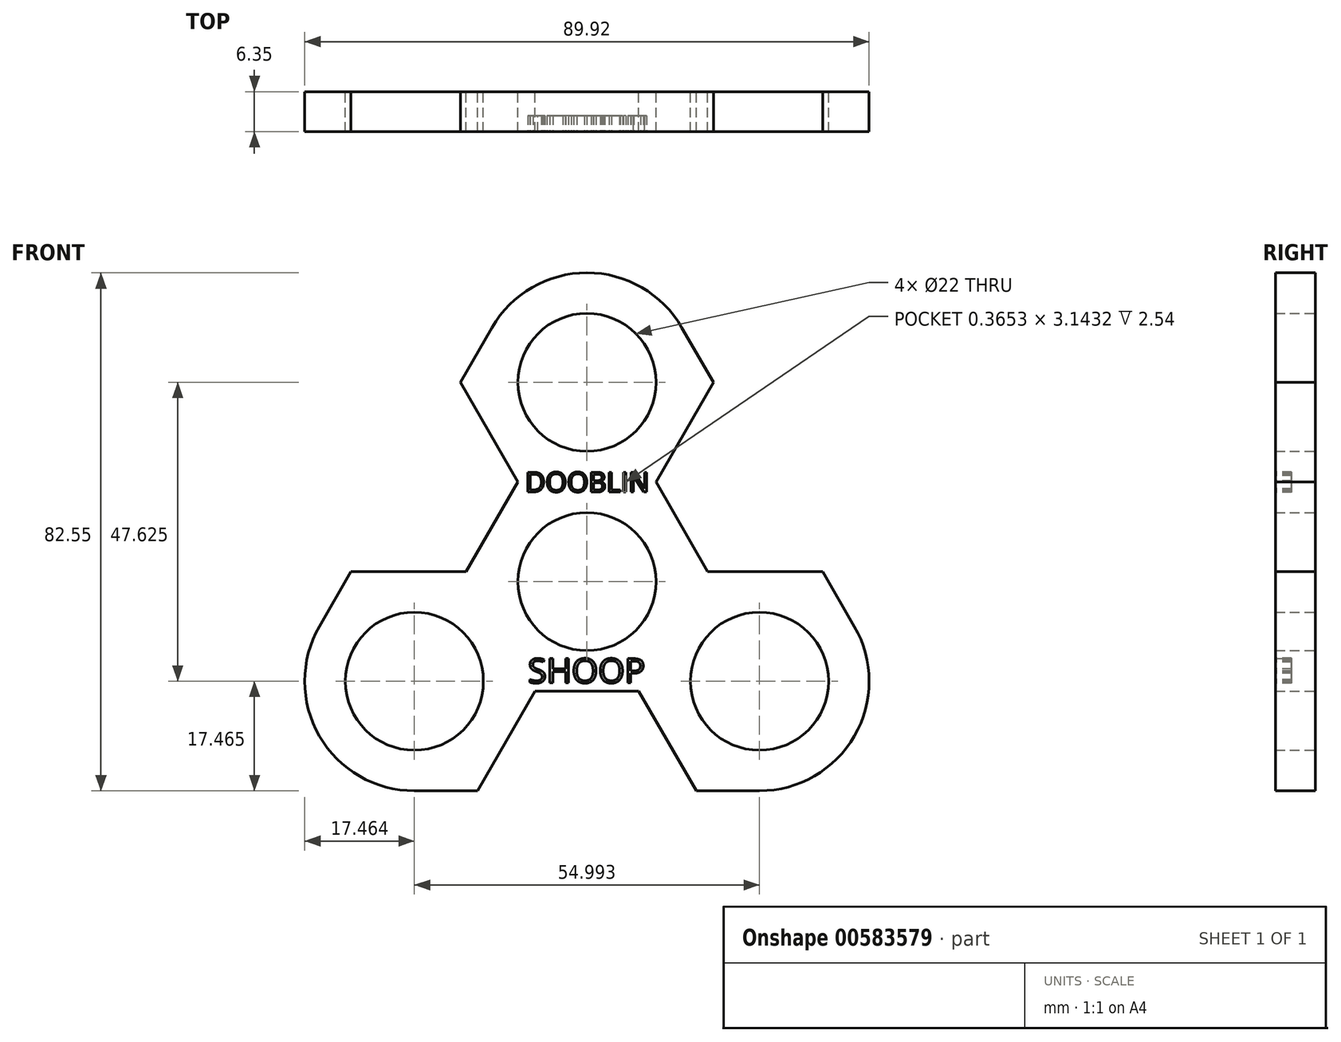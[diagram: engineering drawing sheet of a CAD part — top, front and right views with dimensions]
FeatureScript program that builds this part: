
annotation { "Feature Type Name" : "Feature", "Feature Type Description" : "" }
export const myFeature = defineFeature(function(context is Context, id is Id, definition is map)
    precondition{}
    {
        {
            var Q0;
            Q0=qCreatedBy(makeId("Front.planeOp"),FACE);
            var sketch = newSketch(context, id + "F0", { "sketchPlane" : qUnion([Q0])});
            skCircle(sketch, "E0", {"center": v(0, 0) * mm, "radius": 11 * mm});
            skCircle(sketch, "E1", {"center": v(0, 0) * mm, "radius": 14.29 * mm});
            skLineSegment(sketch, "E2", {"start": v(0, 0) * mm, "end": v(0, 31.75) * mm});
            skCircle(sketch, "E3", {"center": v(0, 31.75) * mm, "radius": 11 * mm});
            skCircle(sketch, "E4", {"center": v(0, 31.75) * mm, "radius": 14.29 * mm});
            skCircle(sketch, "E5.1.0", {"center": v(-27.5, -15.87) * mm, "radius": 11 * mm});
            skCircle(sketch, "E5.1.1", {"center": v(-27.5, -15.87) * mm, "radius": 14.29 * mm});
            skCircle(sketch, "E5.2.0", {"center": v(27.5, -15.88) * mm, "radius": 11 * mm});
            skCircle(sketch, "E5.2.1", {"center": v(27.5, -15.88) * mm, "radius": 14.29 * mm});
            skSolve(sketch);
        }
        {
            var Q0;
            Q0=qCreatedBy(makeId("Front.planeOp"),FACE);
            var sketch = newSketch(context, id + "F1", { "sketchPlane" : qUnion([Q0])});
            skCircle(sketch, "E6.0", {"center": v(0, 31.75) * mm, "radius": 14.29 * mm});
            skCircle(sketch, "E7.0", {"center": v(-27.5, -15.87) * mm, "radius": 14.29 * mm});
            skCircle(sketch, "E8.0", {"center": v(27.5, -15.88) * mm, "radius": 14.29 * mm});
            skCircle(sketch, "E9.0", {"center": v(0, 0) * mm, "radius": 14.29 * mm});
            skLineSegment(sketch, "E10.0", {"start": v(-10.08, 17.46) * mm, "end": v(-10.04, 17.46) * mm});
            skLineSegment(sketch, "E10.1", {"start": v(11, 15.88) * mm, "end": v(19.25, 1.59) * mm});
            skLineSegment(sketch, "E10.2", {"start": v(20.16, 0) * mm, "end": v(20.14, -0.04) * mm});
            skLineSegment(sketch, "E10.3", {"start": v(8.25, -17.46) * mm, "end": v(-8.25, -17.46) * mm});
            skLineSegment(sketch, "E10.4", {"start": v(-10.08, -17.46) * mm, "end": v(-10.1, -17.43) * mm});
            skLineSegment(sketch, "E10.5", {"start": v(-19.25, 1.59) * mm, "end": v(-11, 15.87) * mm});
            skPoint(sketch, "E10.0.midPoint", {"position": v(0, 17.46) * mm});
            skLineSegment(sketch, "E11.0", {"start": v(10.08, 14.29) * mm, "end": v(10.04, 14.29) * mm});
            skLineSegment(sketch, "E11.1", {"start": v(-11, 15.87) * mm, "end": v(-20.16, 31.75) * mm});
            skLineSegment(sketch, "E11.2", {"start": v(-20.16, 31.75) * mm, "end": v(-10.08, 49.21) * mm});
            skLineSegment(sketch, "E11.3", {"start": v(-10.08, 49.21) * mm, "end": v(10.08, 49.21) * mm});
            skLineSegment(sketch, "E11.4", {"start": v(10.08, 49.21) * mm, "end": v(20.16, 31.75) * mm});
            skLineSegment(sketch, "E11.5", {"start": v(20.16, 31.75) * mm, "end": v(11, 15.88) * mm});
            skPoint(sketch, "E11.0.midPoint", {"position": v(0, 14.29) * mm});
            skLineSegment(sketch, "E12.0", {"start": v(-17.41, 1.59) * mm, "end": v(-17.4, 1.55) * mm});
            skLineSegment(sketch, "E12.1", {"start": v(-8.25, -17.46) * mm, "end": v(-17.41, -33.34) * mm});
            skLineSegment(sketch, "E12.2", {"start": v(-17.41, -33.34) * mm, "end": v(-37.58, -33.34) * mm});
            skLineSegment(sketch, "E12.3", {"start": v(-37.58, -33.34) * mm, "end": v(-47.66, -15.88) * mm});
            skLineSegment(sketch, "E12.4", {"start": v(-47.66, -15.88) * mm, "end": v(-37.58, 1.59) * mm});
            skLineSegment(sketch, "E12.5", {"start": v(-37.58, 1.59) * mm, "end": v(-19.25, 1.59) * mm});
            skPoint(sketch, "E12.0.midPoint", {"position": v(-12.37, -7.14) * mm});
            skLineSegment(sketch, "E13.0", {"start": v(7.33, -15.88) * mm, "end": v(7.35, -15.84) * mm});
            skLineSegment(sketch, "E13.1", {"start": v(19.25, 1.59) * mm, "end": v(37.58, 1.59) * mm});
            skLineSegment(sketch, "E13.2", {"start": v(37.58, 1.59) * mm, "end": v(47.66, -15.88) * mm});
            skLineSegment(sketch, "E13.3", {"start": v(47.66, -15.88) * mm, "end": v(37.58, -33.34) * mm});
            skLineSegment(sketch, "E13.4", {"start": v(37.58, -33.34) * mm, "end": v(17.41, -33.34) * mm});
            skLineSegment(sketch, "E13.5", {"start": v(17.41, -33.34) * mm, "end": v(8.25, -17.46) * mm});
            skPoint(sketch, "E13.0.midPoint", {"position": v(12.37, -7.14) * mm});
            skLineSegment(sketch, "E14.trimOffspring", {"start": v(-10.04, 14.29) * mm, "end": v(-10.08, 14.29) * mm});
            skLineSegment(sketch, "E15.trimOffspring", {"start": v(10.04, 17.46) * mm, "end": v(10.08, 17.46) * mm});
            skLineSegment(sketch, "E16.trimOffspring", {"start": v(10.1, -17.43) * mm, "end": v(10.08, -17.46) * mm});
            skLineSegment(sketch, "E17.trimOffspring", {"start": v(17.4, 1.55) * mm, "end": v(17.41, 1.59) * mm});
            skLineSegment(sketch, "E18.trimOffspring", {"start": v(-20.14, -0.04) * mm, "end": v(-20.16, 0) * mm});
            skLineSegment(sketch, "E19.trimOffspring", {"start": v(-7.35, -15.84) * mm, "end": v(-7.33, -15.87) * mm});
            skSolve(sketch);
        }
        {
            var Q0;
            Q0 = qSketchRegion(id + "F1", true);
            extrude(context, id + "F2", {"entities" : qUnion([Q0]), "depth" : 6.35 * mm, "offsetDistance" : 25.4 * mm});
        }
        {
            var Q0;
            Q0=makeQuery(id+"F2.opExtrude","CAP_FACE",FACE,{"disambiguationData":[OSD([sQuery(id+"F1.wireOp",EDGE,"E6.0"),sQuery(id+"F1.wireOp",EDGE,"E7.0"),sQuery(id+"F1.wireOp",EDGE,"E8.0"),sQuery(id+"F1.wireOp",EDGE,"E9.0"),sQuery(id+"F1.wireOp",EDGE,"E10.1"),sQuery(id+"F1.wireOp",EDGE,"E10.3"),sQuery(id+"F1.wireOp",EDGE,"E10.5"),sQuery(id+"F1.wireOp",EDGE,"E11.1"),sQuery(id+"F1.wireOp",EDGE,"E11.2"),sQuery(id+"F1.wireOp",EDGE,"E11.3"),sQuery(id+"F1.wireOp",EDGE,"E11.4"),sQuery(id+"F1.wireOp",EDGE,"E11.5"),sQuery(id+"F1.wireOp",EDGE,"E12.1"),sQuery(id+"F1.wireOp",EDGE,"E12.2"),sQuery(id+"F1.wireOp",EDGE,"E12.3"),sQuery(id+"F1.wireOp",EDGE,"E12.4"),sQuery(id+"F1.wireOp",EDGE,"E12.5"),sQuery(id+"F1.wireOp",EDGE,"E13.1"),sQuery(id+"F1.wireOp",EDGE,"E13.2"),sQuery(id+"F1.wireOp",EDGE,"E13.3"),sQuery(id+"F1.wireOp",EDGE,"E13.4"),sQuery(id+"F1.wireOp",EDGE,"E13.5")])],"isStart":false});
            var sketch = newSketch(context, id + "F3", { "sketchPlane" : qUnion([Q0])});
            skText(sketch, "E20", { "text": "DOOBLIN", "fontName": "OpenSans-Regular.ttf"});
            skLineSegment(sketch, "E21", {"start": v(0, 15.88) * mm, "end": v(0, 15.88) * mm});
            skLineSegment(sketch, "E22", {"start": v(0, 14.29) * mm, "end": v(0, 17.46) * mm});
            skLineSegment(sketch, "E23", {"start": v(0, 17.46) * mm, "end": v(0, 14.29) * mm});
            skLineSegment(sketch, "E24", {"start": v(0, 14.29) * mm, "end": v(0, 12.01) * mm});
            skLineSegment(sketch, "E25", {"start": v(0, 12.01) * mm, "end": v(0, 17.46) * mm});
            skLineSegment(sketch, "E26.0", {"start": v(0, 0) * mm, "end": v(0, 31.75) * mm});
            const initialGuessF3  = {"E20": [-0.00982, 0.01429, 1, 0, 0.00317]};
            skSetInitialGuess(sketch, initialGuessF3);
            skSolve(sketch);
        }
        {
            var Q0;
            Q0 = qSketchRegion(id + "F3", true);
            extrude(context, id + "F4", {"entities" : qUnion([Q0]), "operationType" : NewBodyOperationType.REMOVE, "oppositeDirection" : true, "depth" : 2.54 * mm, "offsetDistance" : 25.4 * mm});
        }
        {
            var Q0;
            {var subQ0=sQuery(id+"F1.wireOp",EDGE,"E13.5");var subQ1=sQuery(id+"F1.wireOp",EDGE,"E13.4");var subQ2=sQuery(id+"F1.wireOp",EDGE,"E13.3");var subQ3=sQuery(id+"F1.wireOp",EDGE,"E12.5");var subQ4=sQuery(id+"F1.wireOp",EDGE,"E11.2");var subQ5=sQuery(id+"F1.wireOp",EDGE,"E11.1");var subQ6=sQuery(id+"F1.wireOp",EDGE,"E10.5");var subQ7=sQuery(id+"F1.wireOp",EDGE,"E10.3");var subQ8=sQuery(id+"F1.wireOp",EDGE,"E10.1");var subQ9=sQuery(id+"F1.wireOp",EDGE,"E11.3");var subQ10=sQuery(id+"F1.wireOp",EDGE,"E6.0");var subQ11=sQuery(id+"F1.wireOp",EDGE,"E9.0");var subQ12=sQuery(id+"F1.wireOp",EDGE,"E7.0");var subQ13=sQuery(id+"F1.wireOp",EDGE,"E8.0");var subQ14=sQuery(id+"F1.wireOp",EDGE,"E11.4");var subQ15=sQuery(id+"F1.wireOp",EDGE,"E11.5");var subQ16=sQuery(id+"F1.wireOp",EDGE,"E12.1");var subQ17=sQuery(id+"F1.wireOp",EDGE,"E12.2");var subQ18=sQuery(id+"F1.wireOp",EDGE,"E12.3");var subQ19=sQuery(id+"F1.wireOp",EDGE,"E12.4");var subQ20=sQuery(id+"F1.wireOp",EDGE,"E13.1");var subQ21=sQuery(id+"F1.wireOp",EDGE,"E13.2");Q0=makeQuery(id+"F4.boolean.opBoolean","SPLIT",FACE,{"disambiguationData":[TD([makeQuery(id+"F2.opExtrude","SWEPT_FACE",FACE,{"disambiguationData":[OSD([subQ10])]})])],"derivedFrom":makeQuery(id+"F2.opExtrude","CAP_FACE",FACE,{"disambiguationData":[OSD([subQ10,subQ12,subQ13,subQ11,subQ8,subQ7,subQ6,subQ5,subQ4,subQ9,subQ14,subQ15,subQ16,subQ17,subQ18,subQ19,subQ3,subQ20,subQ21,subQ2,subQ1,subQ0])],"isStart":false})});}
            var sketch = newSketch(context, id + "F5", { "sketchPlane" : qUnion([Q0])});
            skCircle(sketch, "E27", {"center": v(0, 31.75) * mm, "radius": 17.46 * mm});
            skCircle(sketch, "E28", {"center": v(-27.5, -15.87) * mm, "radius": 17.46 * mm});
            skCircle(sketch, "E29", {"center": v(27.5, -15.88) * mm, "radius": 17.46 * mm});
            skSolve(sketch);
        }
        {
            var Q0;
            {var subQ0=sQuery(id+"F5.wireOp",EDGE,"E27");var subQ1=makeQuery(id+"F2.opExtrude","CAP_EDGE",EDGE,{"disambiguationData":[OSD([sQuery(id+"F1.wireOp",EDGE,"E11.3")])],"isStart":false});var subQ2=makeQuery(id+"F5.imprint","INTERSECT",VERTEX,{"derivedFrom":[subQ1,subQ0]});Q0=makeQuery(id+"F5.imprint","IMPRINT",FACE,{"disambiguationData":[TD([[makeQuery(id+"F5.imprint","IMPRINT",EDGE,{"disambiguationData":[TD([[subQ2,-1.0]])],"derivedFrom":subQ0}),-1.0]])]});}
            var Q1;
            {var subQ0=sQuery(id+"F5.wireOp",EDGE,"E27");var subQ1=makeQuery(id+"F2.opExtrude","CAP_EDGE",EDGE,{"disambiguationData":[OSD([sQuery(id+"F1.wireOp",EDGE,"E11.3")])],"isStart":false});var subQ2=makeQuery(id+"F5.imprint","INTERSECT",VERTEX,{"derivedFrom":[subQ1,subQ0]});Q1=makeQuery(id+"F5.imprint","IMPRINT",FACE,{"disambiguationData":[TD([[makeQuery(id+"F5.imprint","IMPRINT",EDGE,{"disambiguationData":[TD([[subQ2,1.0]])],"derivedFrom":subQ0}),-1.0]])]});}
            var Q2;
            {var subQ0=sQuery(id+"F5.wireOp",EDGE,"E28");var subQ1=makeQuery(id+"F2.opExtrude","CAP_EDGE",EDGE,{"disambiguationData":[OSD([sQuery(id+"F1.wireOp",EDGE,"E12.4")])],"isStart":false});var subQ2=makeQuery(id+"F5.imprint","INTERSECT",VERTEX,{"derivedFrom":[subQ1,subQ0]});Q2=makeQuery(id+"F5.imprint","IMPRINT",FACE,{"disambiguationData":[TD([[makeQuery(id+"F5.imprint","IMPRINT",EDGE,{"disambiguationData":[TD([[subQ2,-1.0]])],"derivedFrom":subQ0}),-1.0]])]});}
            var Q3;
            {var subQ0=sQuery(id+"F5.wireOp",EDGE,"E28");var subQ1=makeQuery(id+"F2.opExtrude","CAP_EDGE",EDGE,{"disambiguationData":[OSD([sQuery(id+"F1.wireOp",EDGE,"E12.3")])],"isStart":false});var subQ2=makeQuery(id+"F5.imprint","INTERSECT",VERTEX,{"derivedFrom":[subQ1,subQ0]});Q3=makeQuery(id+"F5.imprint","IMPRINT",FACE,{"disambiguationData":[TD([[makeQuery(id+"F5.imprint","IMPRINT",EDGE,{"disambiguationData":[TD([[subQ2,-1.0]])],"derivedFrom":subQ0}),-1.0]])]});}
            var Q4;
            {var subQ0=sQuery(id+"F5.wireOp",EDGE,"E29");var subQ1=makeQuery(id+"F2.opExtrude","CAP_EDGE",EDGE,{"disambiguationData":[OSD([sQuery(id+"F1.wireOp",EDGE,"E13.4")])],"isStart":false});var subQ2=makeQuery(id+"F5.imprint","INTERSECT",VERTEX,{"derivedFrom":[subQ1,subQ0]});Q4=makeQuery(id+"F5.imprint","IMPRINT",FACE,{"disambiguationData":[TD([[makeQuery(id+"F5.imprint","IMPRINT",EDGE,{"disambiguationData":[TD([[subQ2,-1.0]])],"derivedFrom":subQ0}),-1.0]])]});}
            var Q5;
            {var subQ0=sQuery(id+"F5.wireOp",EDGE,"E29");var subQ1=makeQuery(id+"F2.opExtrude","CAP_EDGE",EDGE,{"disambiguationData":[OSD([sQuery(id+"F1.wireOp",EDGE,"E13.2")])],"isStart":false});var subQ2=makeQuery(id+"F5.imprint","INTERSECT",VERTEX,{"derivedFrom":[subQ1,subQ0]});Q5=makeQuery(id+"F5.imprint","IMPRINT",FACE,{"disambiguationData":[TD([[makeQuery(id+"F5.imprint","IMPRINT",EDGE,{"disambiguationData":[TD([[subQ2,1.0]])],"derivedFrom":subQ0}),-1.0]])]});}
            extrude(context, id + "F6", {"entities" : qUnion([Q0, Q1, Q2, Q3, Q4, Q5]), "operationType" : NewBodyOperationType.REMOVE, "oppositeDirection" : true, "depth" : 25.4 * mm, "offsetDistance" : 25.4 * mm});
        }
        {
            var Q0;
            Q0=makeQuery(id+"F0.imprint","IMPRINT",FACE,{"disambiguationData":[TD([[makeQuery(id+"F0.imprint","IMPRINT",EDGE,{"derivedFrom":sQuery(id+"F0.wireOp",EDGE,"E3")}),-1.0]])]});
            var sketch = newSketch(context, id + "F7", { "sketchPlane" : qUnion([Q0])});
            skSolve(sketch);
        }
        {
            var Q0;
            Q0 = qSketchRegion(id + "F7", true);
            var Q1;
            Q1=makeQuery(id+"F0.imprint","IMPRINT",FACE,{"disambiguationData":[TD([[makeQuery(id+"F0.imprint","IMPRINT",EDGE,{"derivedFrom":sQuery(id+"F0.wireOp",EDGE,"E5.1.0")}),-1.0]])]});
            var Q2;
            Q2=makeQuery(id+"F0.imprint","IMPRINT",FACE,{"disambiguationData":[TD([[makeQuery(id+"F0.imprint","IMPRINT",EDGE,{"derivedFrom":sQuery(id+"F0.wireOp",EDGE,"E0")}),-1.0]])]});
            var Q3;
            Q3=makeQuery(id+"F0.imprint","IMPRINT",FACE,{"disambiguationData":[TD([[makeQuery(id+"F0.imprint","IMPRINT",EDGE,{"derivedFrom":sQuery(id+"F0.wireOp",EDGE,"E5.2.0")}),-1.0]])]});
            var Q4;
            Q4=makeQuery(id+"F0.imprint","IMPRINT",FACE,{"disambiguationData":[TD([[makeQuery(id+"F0.imprint","IMPRINT",EDGE,{"derivedFrom":sQuery(id+"F0.wireOp",EDGE,"E3")}),-1.0]])]});
            extrude(context, id + "F8", {"entities" : qUnion([Q0, Q1, Q2, Q3, Q4]), "operationType" : NewBodyOperationType.ADD, "depth" : 6.35 * mm, "offsetDistance" : 25.4 * mm});
        }
        {
            var Q0;
            {var subQ0=sQuery(id+"F1.wireOp",EDGE,"E13.5");var subQ1=sQuery(id+"F1.wireOp",EDGE,"E13.4");var subQ2=sQuery(id+"F1.wireOp",EDGE,"E13.3");var subQ3=sQuery(id+"F1.wireOp",EDGE,"E12.5");var subQ4=sQuery(id+"F1.wireOp",EDGE,"E11.2");var subQ5=sQuery(id+"F1.wireOp",EDGE,"E11.1");var subQ6=sQuery(id+"F1.wireOp",EDGE,"E10.5");var subQ7=sQuery(id+"F1.wireOp",EDGE,"E10.3");var subQ8=sQuery(id+"F1.wireOp",EDGE,"E10.1");var subQ9=sQuery(id+"F1.wireOp",EDGE,"E11.3");var subQ10=sQuery(id+"F1.wireOp",EDGE,"E6.0");var subQ11=sQuery(id+"F1.wireOp",EDGE,"E9.0");var subQ12=sQuery(id+"F1.wireOp",EDGE,"E7.0");var subQ13=sQuery(id+"F1.wireOp",EDGE,"E8.0");var subQ14=sQuery(id+"F1.wireOp",EDGE,"E11.4");var subQ15=sQuery(id+"F1.wireOp",EDGE,"E11.5");var subQ16=sQuery(id+"F1.wireOp",EDGE,"E12.1");var subQ17=sQuery(id+"F1.wireOp",EDGE,"E12.2");var subQ18=sQuery(id+"F1.wireOp",EDGE,"E12.3");var subQ19=sQuery(id+"F1.wireOp",EDGE,"E12.4");var subQ20=sQuery(id+"F1.wireOp",EDGE,"E13.1");var subQ21=sQuery(id+"F1.wireOp",EDGE,"E13.2");Q0=makeQuery(id+"F8.boolean.opBoolean","MERGE",FACE,{"derivedFrom":[makeQuery(id+"F4.boolean.opBoolean","SPLIT",FACE,{"disambiguationData":[TD([makeQuery(id+"F2.opExtrude","SWEPT_FACE",FACE,{"disambiguationData":[OSD([subQ10])]})])],"derivedFrom":makeQuery(id+"F2.opExtrude","CAP_FACE",FACE,{"disambiguationData":[OSD([subQ10,subQ12,subQ13,subQ11,subQ8,subQ7,subQ6,subQ5,subQ4,subQ9,subQ14,subQ15,subQ16,subQ17,subQ18,subQ19,subQ3,subQ20,subQ21,subQ2,subQ1,subQ0])],"isStart":false})}),makeQuery(id+"F8.opExtrude","CAP_FACE",FACE,{"disambiguationData":[OSD([sQuery(id+"F0.wireOp",EDGE,"E0"),sQuery(id+"F0.wireOp",EDGE,"E1")])],"isStart":false}),makeQuery(id+"F8.opExtrude","CAP_FACE",FACE,{"disambiguationData":[OSD([sQuery(id+"F0.wireOp",EDGE,"E3"),sQuery(id+"F0.wireOp",EDGE,"E4")])],"isStart":false}),makeQuery(id+"F8.opExtrude","CAP_FACE",FACE,{"disambiguationData":[OSD([sQuery(id+"F0.wireOp",EDGE,"E5.1.0"),sQuery(id+"F0.wireOp",EDGE,"E5.1.1")])],"isStart":false}),makeQuery(id+"F8.opExtrude","CAP_FACE",FACE,{"disambiguationData":[OSD([sQuery(id+"F0.wireOp",EDGE,"E5.2.0"),sQuery(id+"F0.wireOp",EDGE,"E5.2.1")])],"isStart":false})]});}
            var sketch = newSketch(context, id + "F9", { "sketchPlane" : qUnion([Q0])});
            skText(sketch, "E30", { "text": "SHOOP\n\n", "fontName": "OpenSans-Regular.ttf"});
            skPoint(sketch, "E31.end.orphan", {"position": v(9.53, -12.23) * mm});
            const initialGuessF9  = {"E30": [-0.0094, -0.01614, 1, 0, 0.0039]};
            skSetInitialGuess(sketch, initialGuessF9);
            skSolve(sketch);
        }
        {
            var Q0;
            Q0 = qSketchRegion(id + "F9", true);
            extrude(context, id + "F10", {"entities" : qUnion([Q0]), "operationType" : NewBodyOperationType.REMOVE, "oppositeDirection" : true, "depth" : 2.54 * mm, "offsetDistance" : 25.4 * mm});
        }
    });
